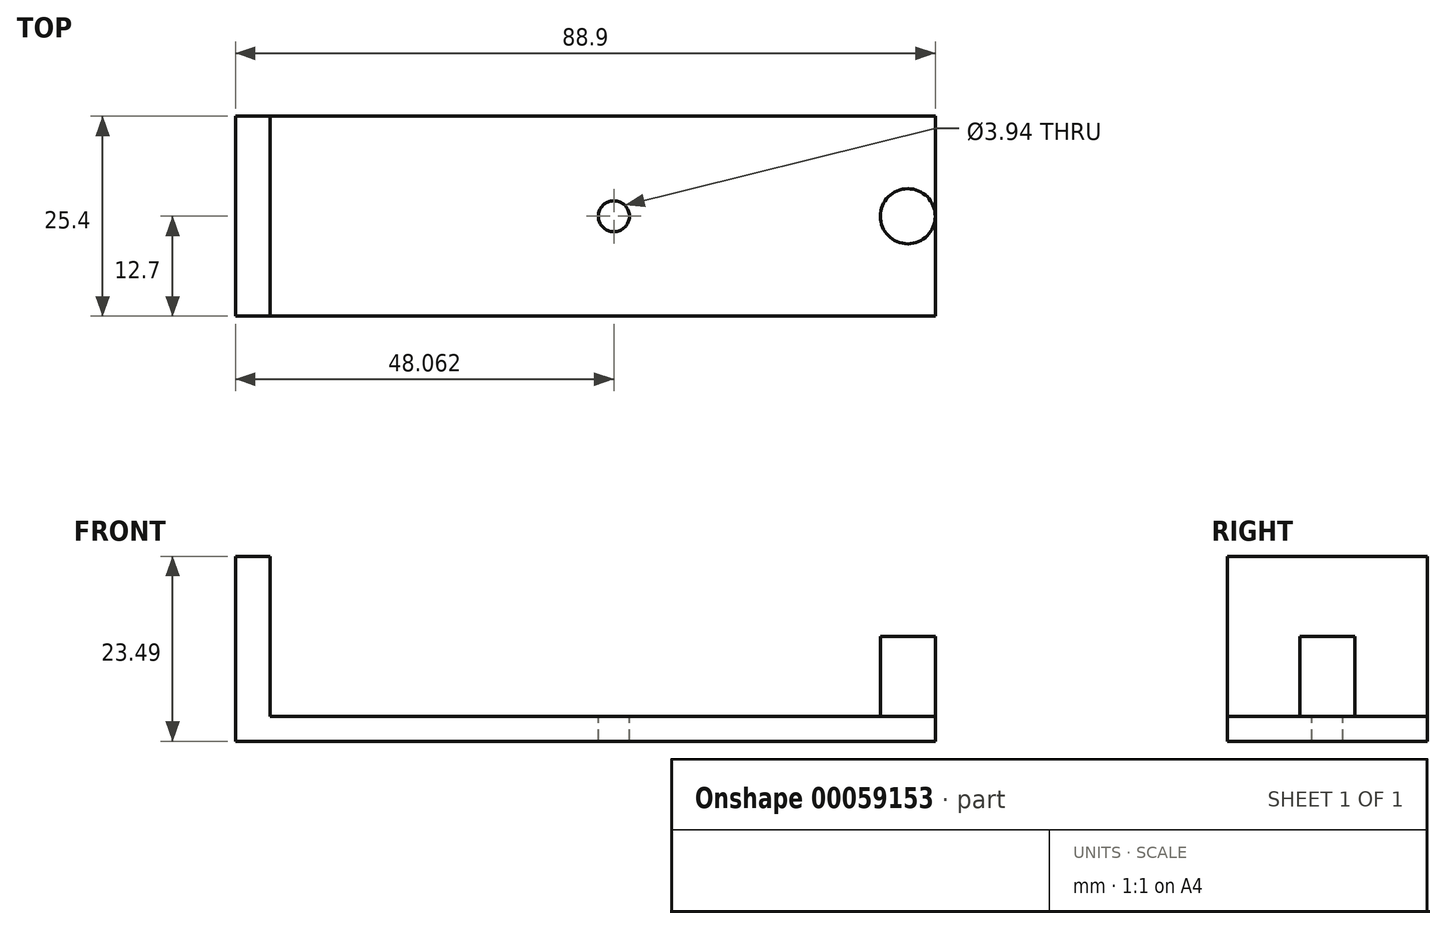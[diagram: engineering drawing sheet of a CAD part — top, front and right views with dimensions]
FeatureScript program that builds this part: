
annotation { "Feature Type Name" : "Feature", "Feature Type Description" : "" }
export const myFeature = defineFeature(function(context is Context, id is Id, definition is map)
    precondition{}
    {
        {
            var Q0;
            Q0=qCreatedBy(makeId("Top.planeOp"),FACE);
            var sketch = newSketch(context, id + "F0", { "sketchPlane" : qUnion([Q0])});
            skLineSegment(sketch, "E0.bottom", {"start": v(-44.45, 12.7) * mm, "end": v(44.45, 12.7) * mm});
            skLineSegment(sketch, "E0.top", {"start": v(-44.45, -12.7) * mm, "end": v(44.45, -12.7) * mm});
            skLineSegment(sketch, "E0.left", {"start": v(-44.45, 12.7) * mm, "end": v(-44.45, -12.7) * mm});
            skLineSegment(sketch, "E0.right", {"start": v(44.45, 12.7) * mm, "end": v(44.45, -12.7) * mm});
            skSolve(sketch);
        }
        {
            var Q0;
            Q0=makeQuery(id+"F0.imprint","IMPRINT",FACE,{"disambiguationData":[TD([[makeQuery(id+"F0.imprint","IMPRINT",EDGE,{"derivedFrom":sQuery(id+"F0.wireOp",EDGE,"E0.bottom")}),-1.0]])]});
            extrude(context, id + "F1", {"entities" : qUnion([Q0]), "depth" : 3.17 * mm});
        }
        {
            var Q0;
            Q0=makeQuery(id+"F1.opExtrude","CAP_FACE",FACE,{"disambiguationData":[OSD([sQuery(id+"F0.wireOp",EDGE,"E0.bottom"),sQuery(id+"F0.wireOp",EDGE,"E0.top"),sQuery(id+"F0.wireOp",EDGE,"E0.left"),sQuery(id+"F0.wireOp",EDGE,"E0.right")])],"isStart":false});
            var sketch = newSketch(context, id + "F2", { "sketchPlane" : qUnion([Q0])});
            skCircle(sketch, "E1", {"center": v(40.95, 0) * mm, "radius": 3.5 * mm});
            skSolve(sketch);
        }
        {
            var Q0;
            Q0=makeQuery(id+"F2.imprint","IMPRINT",FACE,{"disambiguationData":[TD([[makeQuery(id+"F2.imprint","IMPRINT",EDGE,{"derivedFrom":sQuery(id+"F2.wireOp",EDGE,"E1")}),1.0]])]});
            extrude(context, id + "F3", {"entities" : qUnion([Q0]), "operationType" : NewBodyOperationType.ADD, "depth" : 10.16 * mm});
        }
        {
            var Q0;
            Q0=makeQuery(id+"F1.opExtrude","CAP_FACE",FACE,{"disambiguationData":[OSD([sQuery(id+"F0.wireOp",EDGE,"E0.bottom"),sQuery(id+"F0.wireOp",EDGE,"E0.top"),sQuery(id+"F0.wireOp",EDGE,"E0.left"),sQuery(id+"F0.wireOp",EDGE,"E0.right")])],"isStart":false});
            var sketch = newSketch(context, id + "F4", { "sketchPlane" : qUnion([Q0])});
            skCircle(sketch, "E2", {"center": v(3.61, 0) * mm, "radius": 1.97 * mm});
            skCircle(sketch, "E3.0", {"center": v(40.95, 0) * mm, "radius": 3.5 * mm});
            skSolve(sketch);
        }
        {
            var Q0;
            Q0=makeQuery(id+"F4.imprint","IMPRINT",FACE,{"disambiguationData":[TD([[makeQuery(id+"F4.imprint","IMPRINT",EDGE,{"derivedFrom":sQuery(id+"F4.wireOp",EDGE,"E2")}),1.0]])]});
            extrude(context, id + "F5", {"entities" : qUnion([Q0]), "operationType" : NewBodyOperationType.REMOVE, "oppositeDirection" : true, "depth" : 25.4 * mm});
        }
        {
            var Q0;
            Q0=makeQuery(id+"F1.opExtrude","CAP_FACE",FACE,{"disambiguationData":[OSD([sQuery(id+"F0.wireOp",EDGE,"E0.bottom"),sQuery(id+"F0.wireOp",EDGE,"E0.top"),sQuery(id+"F0.wireOp",EDGE,"E0.left"),sQuery(id+"F0.wireOp",EDGE,"E0.right")])],"isStart":false});
            var sketch = newSketch(context, id + "F6", { "sketchPlane" : qUnion([Q0])});
            skLineSegment(sketch, "E4.bottom", {"start": v(-44.45, -12.7) * mm, "end": v(-40.08, -12.7) * mm});
            skLineSegment(sketch, "E4.top", {"start": v(-44.45, 12.7) * mm, "end": v(-40.08, 12.7) * mm});
            skLineSegment(sketch, "E4.left", {"start": v(-44.45, -12.7) * mm, "end": v(-44.45, 12.7) * mm});
            skLineSegment(sketch, "E4.right", {"start": v(-40.08, -12.7) * mm, "end": v(-40.08, 12.7) * mm});
            skCircle(sketch, "E5.0", {"center": v(3.61, 0) * mm, "radius": 1.97 * mm});
            skSolve(sketch);
        }
        {
            var Q0;
            Q0=makeQuery(id+"F6.imprint","IMPRINT",FACE,{"disambiguationData":[TD([[makeQuery(id+"F6.imprint","IMPRINT",EDGE,{"derivedFrom":sQuery(id+"F6.wireOp",EDGE,"E4.bottom")}),1.0]])]});
            extrude(context, id + "F7", {"entities" : qUnion([Q0]), "operationType" : NewBodyOperationType.ADD, "depth" : 20.32 * mm});
        }
    });
